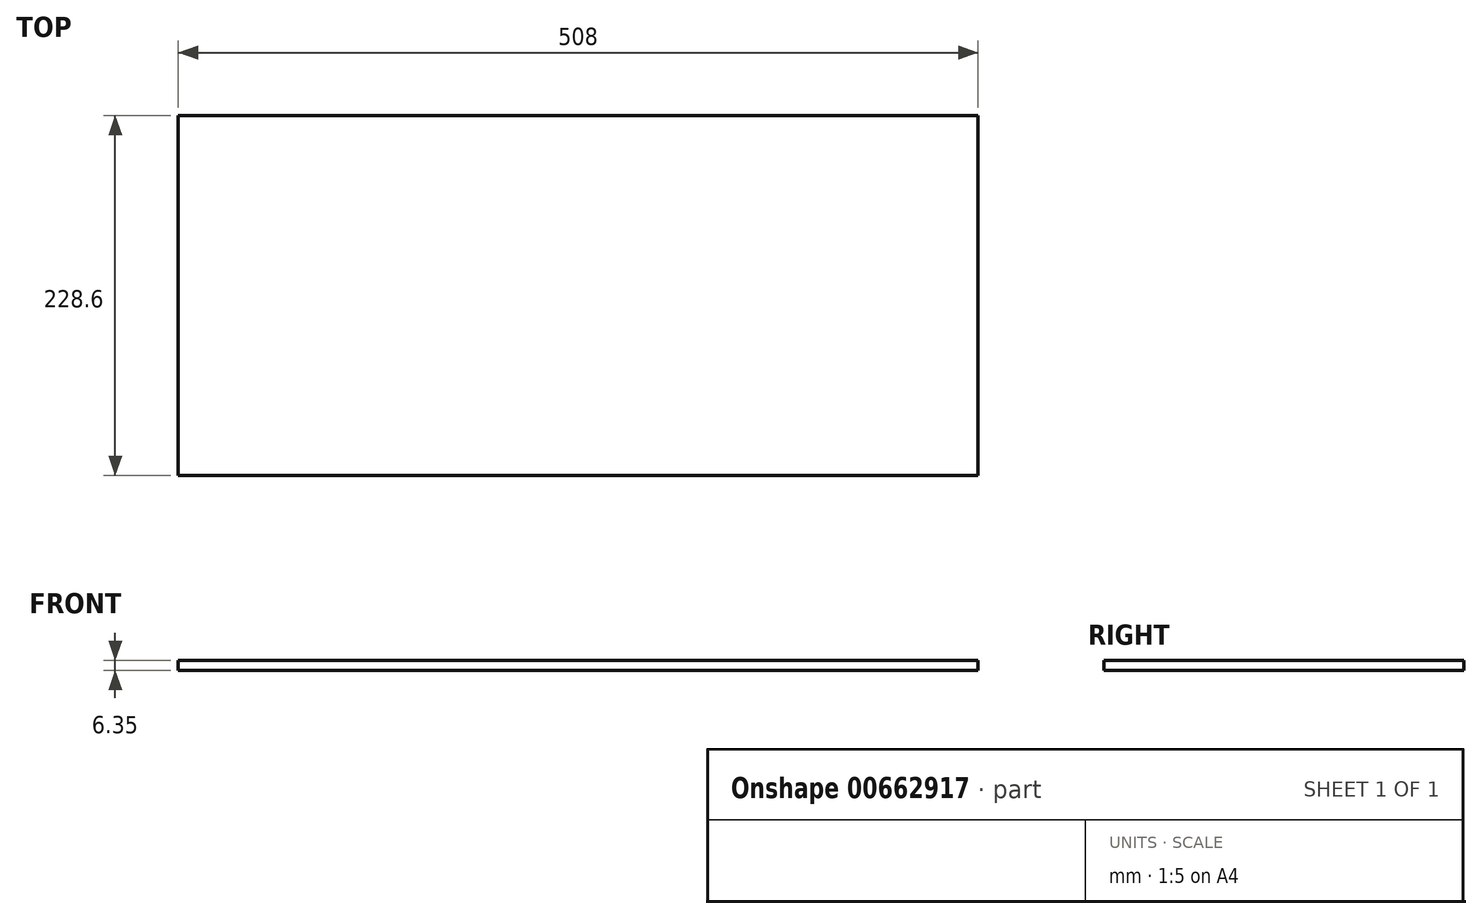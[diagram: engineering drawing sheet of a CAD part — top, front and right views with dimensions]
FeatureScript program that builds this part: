
annotation { "Feature Type Name" : "Feature", "Feature Type Description" : "" }
export const myFeature = defineFeature(function(context is Context, id is Id, definition is map)
    precondition{}
    {
        {
            var Q0;
            Q0=qCreatedBy(makeId("Top.planeOp"),FACE);
            var sketch = newSketch(context, id + "F0", { "sketchPlane" : qUnion([Q0])});
            skLineSegment(sketch, "E0.bottom", {"start": v(-244.75, 58.9) * mm, "end": v(263.25, 58.9) * mm});
            skLineSegment(sketch, "E0.top", {"start": v(-244.75, -169.7) * mm, "end": v(263.25, -169.7) * mm});
            skLineSegment(sketch, "E0.left", {"start": v(-244.75, 58.9) * mm, "end": v(-244.75, -169.7) * mm});
            skLineSegment(sketch, "E0.right", {"start": v(263.25, 58.9) * mm, "end": v(263.25, -169.7) * mm});
            skSolve(sketch);
        }
        {
            var Q0;
            Q0=makeQuery(id+"F0.imprint","IMPRINT",FACE,{"disambiguationData":[TD([[makeQuery(id+"F0.imprint","IMPRINT",EDGE,{"derivedFrom":sQuery(id+"F0.wireOp",EDGE,"E0.bottom")}),-1.0]])]});
            extrude(context, id + "F1", {"entities" : qUnion([Q0]), "depth" : 6.35 * mm, "offsetDistance" : 25.4 * mm});
        }
    });
